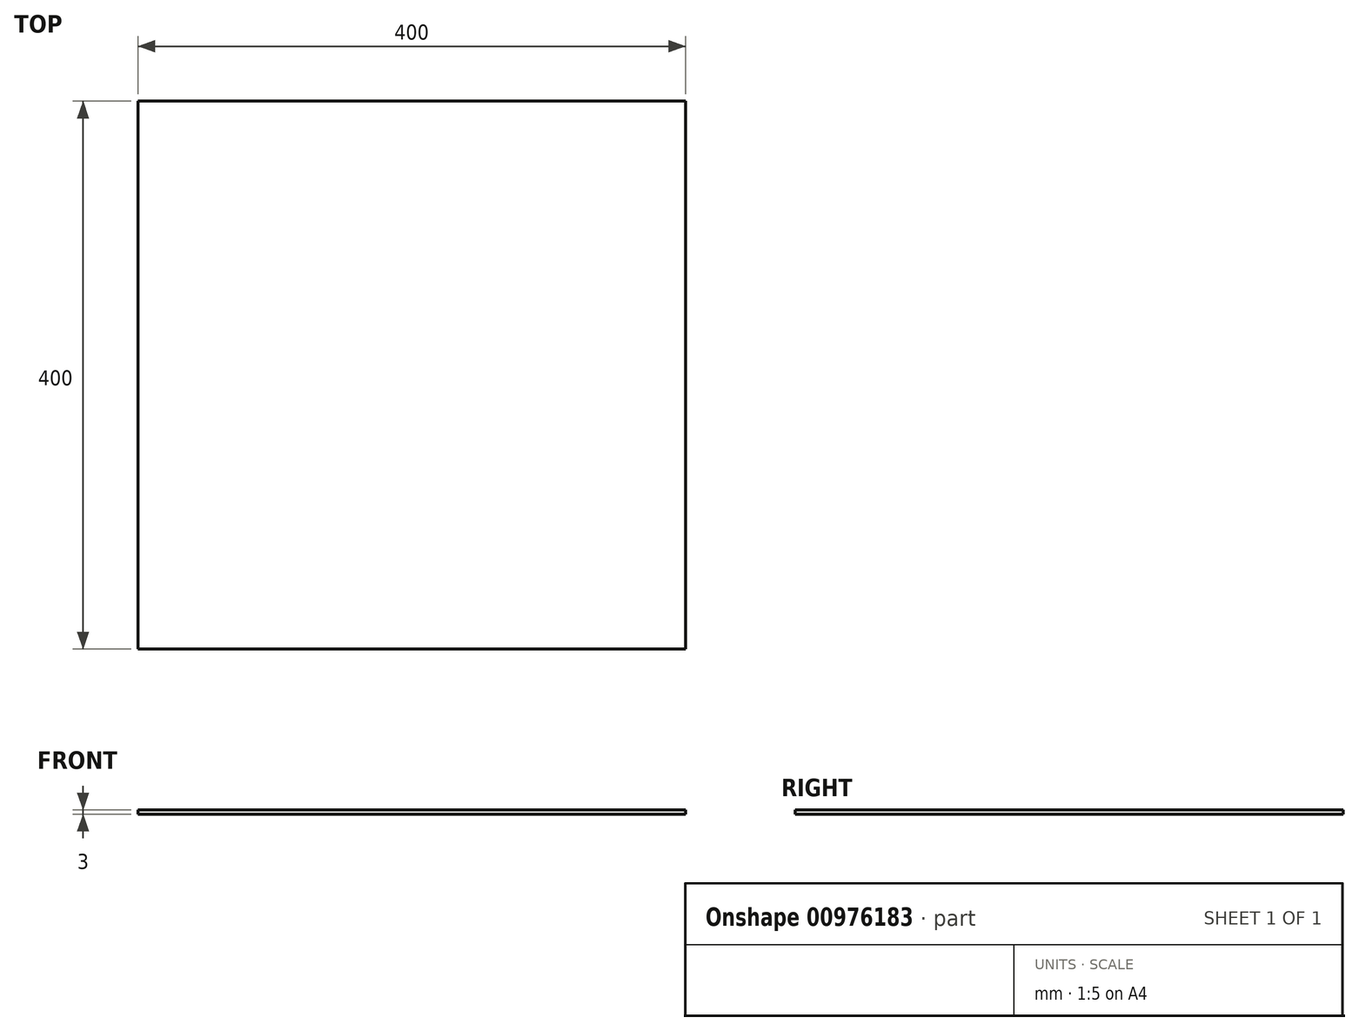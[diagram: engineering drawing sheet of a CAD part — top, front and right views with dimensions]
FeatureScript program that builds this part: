
annotation { "Feature Type Name" : "Feature", "Feature Type Description" : "" }
export const myFeature = defineFeature(function(context is Context, id is Id, definition is map)
    precondition{}
    {
        {
            var Q0;
            Q0=qCreatedBy(makeId("Top.planeOp"),FACE);
            var sketch = newSketch(context, id + "F0", { "sketchPlane" : qUnion([Q0])});
            skLineSegment(sketch, "E0.bottom", {"start": v(-200, -200) * mm, "end": v(200, -200) * mm});
            skLineSegment(sketch, "E0.top", {"start": v(-200, 200) * mm, "end": v(200, 200) * mm});
            skLineSegment(sketch, "E0.left", {"start": v(-200, -200) * mm, "end": v(-200, 200) * mm});
            skLineSegment(sketch, "E0.right", {"start": v(200, -200) * mm, "end": v(200, 200) * mm});
            skPoint(sketch, "E0.middle", {"position": v(0, 0) * mm});
            skSolve(sketch);
        }
        {
            var Q0;
            Q0=makeQuery(id+"F0.imprint","IMPRINT",FACE,{"disambiguationData":[TD([[makeQuery(id+"F0.imprint","IMPRINT",EDGE,{"derivedFrom":sQuery(id+"F0.wireOp",EDGE,"E0.bottom")}),1.0]])]});
            extrude(context, id + "F1", {"entities" : qUnion([Q0]), "depth" : 3 * mm, "offsetDistance" : 25 * mm});
        }
    });
